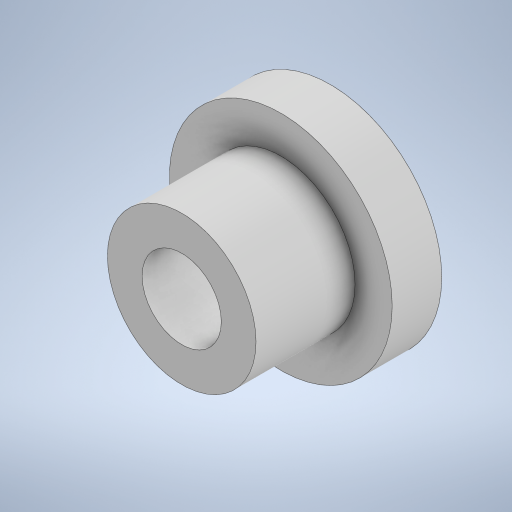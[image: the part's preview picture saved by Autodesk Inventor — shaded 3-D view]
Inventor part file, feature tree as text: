
AUTODESK INVENTOR PART (.ipt)
format: ipt  version: 2024 (Build 280153000, 153)  size: 596,992 bytes
history: native  units: mm
features: other x3, plane x2, extrude x2, sketch x2, reference x1
ambient origin geometry x8: Origin, YZ Plane, XZ Plane, XY Plane, X Axis, Y Axis, Z Axis, Center Point
bodies: Solid1 (feature_tree)
feature tree (10):
  plane  "Work Plane1"
  extrude  "Extrusion1"  Depth=5.6mm
  sketch  "Sketch2"  dims[d2=4.0mm d3=0.0mm d4=12.0mm d5=0.4mm d6=10.0mm d7=0.0mm]
  plane  "Work Plane2"
  extrude  "Extrusion2"  Depth=12.0mm
  sketch  "Sketch1"  dims[d0=18.0mm d1=5.6mm]
  reference  "Reference1"
  other  "<userpath>\Documents\Inventor\robot arm\base_assembly.iam"
  other  "base_assembly.iam"
  other  "base_bearing_Circle:3"
